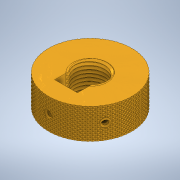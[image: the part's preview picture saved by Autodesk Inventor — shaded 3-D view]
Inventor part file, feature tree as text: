
AUTODESK INVENTOR PART (.ipt)
format: ipt  version: 2020 (Build 240168000, 168)  size: 9,379,328 bytes
history: native  units: in
note: dims shown in document units (in); Inventor stores cm internally (conversion verified against a paired STEP export)
features: sketch x8, helix x3, extrude x2, hole x2, thread x2, revolve x2, pattern_circular x2, plane x1, mirror x1
ambient origin geometry x8: Origin, YZ Plane, XZ Plane, XY Plane, X Axis, Y Axis, Z Axis, Center Point
bodies: Solid1 (feature_tree), Solid2 (feature_tree), Solid3 (feature_tree)
feature tree (23):
  sketch  "Sketch1"  dims[d0=1.375in d1=0.5in d2=0.0in]
  extrude  "Extrusion1"  Depth=0.5in TaperAngle=0.0deg
  hole  "Hole2"  [1 undecoded]
  thread  "Thread1"  [1 undecoded]
  revolve  "Revolution1"  [1 undecoded]
  helix  "Coil1"  [1 undecoded]
  sketch  "Sketch4"  dims[d29=0.0556in d30=0.6111in d31=0.3937in d32=0.0in d33=0.0in d34=0.0in d35=0.0in d36=0.0in d37=0.1875in d38=0.1875in]
  plane  "Work Plane1"
  hole  "Hole3"  [1 undecoded]
  thread  "Thread2"  [1 undecoded]
  revolve  "Revolution2"  Angle=30.0deg
  helix  "Coil2"  [1 undecoded]
  pattern_circular  "Circular Pattern1"  [2 undecoded]
  extrude  "Extrusion3"  Depth=0.3779in
  helix  "Coil3"  [1 undecoded]
  pattern_circular  "Circular Pattern2"  Count=3 Angle=120.0deg
  mirror  "Mirror1"
  sketch  "Sketch2"  dims[d10=0.565in d11=1.25in d12=0.375in d13=0.25in d14=0.5635in d15=1.0in d16=0.0in d17=0.5in d18=0.0in d19=0.3779in d20=0.0089in d21=0.0089in]
  sketch  "Sketch3"  dims[d24=0.0556in d26=0.3779in d28=0.0in]
  sketch  "Sketch5"  dims[d39=0.3059in d42=30.0deg d43=0.25in]
  sketch  "Sketch6"  dims[d44=0.145in d45=0.38in d46=0.375in d47=0.25in d48=0.5635in d49=0.588in d50=0.0in]
  sketch  "Sketch7"  dims[d51=0.414in d52=0.0in]
  sketch  "Sketch8"  dims[d53=0.3779in d54=0.0067in d55=0.0067in d58=0.0417in d60=0.3779in d62=0.0in d63=0.0417in d64=0.4978in d65=0.3937in d66=0.0in d67=0.0in d68=0.0in d69=0.0in d70=0.0in d71=1.1811in d72=120.0deg d74=0.0in d75=0.0in d76=0.0172in d77=0.0305in d78=1.0in d79=0.5in d80=0.0492in d81=0.0in d82=90.0deg d83=90.0deg d84=0.0in d85=0.0in d86=28.3465in d87=360.0deg]
note: 10 required parameter values undecoded (feature->parameter linkage not recoverable at this tier; creation-order binding heuristic only, values carry confidence <= 0.55)